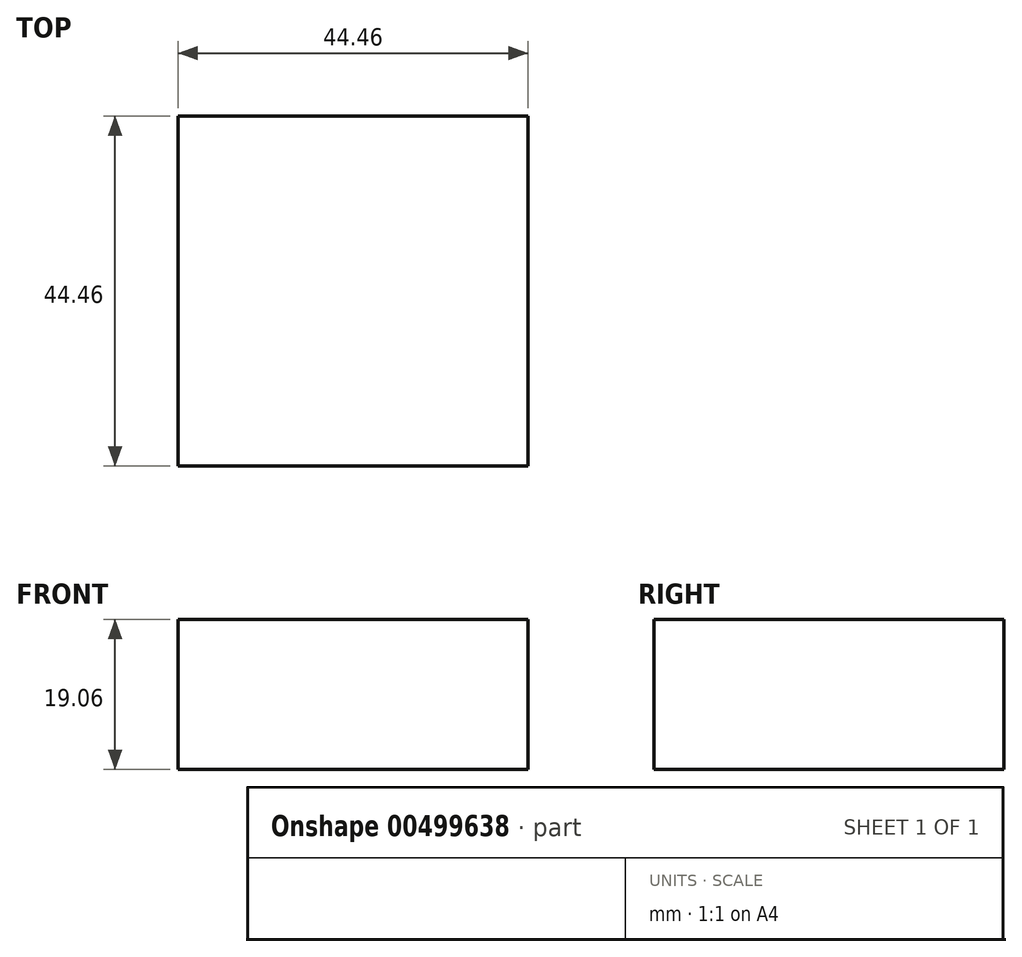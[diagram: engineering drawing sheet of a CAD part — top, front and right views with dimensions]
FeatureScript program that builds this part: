
annotation { "Feature Type Name" : "Feature", "Feature Type Description" : "" }
export const myFeature = defineFeature(function(context is Context, id is Id, definition is map)
    precondition{}
    {
        {
            var Q0;
            Q0=qCreatedBy(makeId("Front.planeOp"),FACE);
            var sketch = newSketch(context, id + "F0", { "sketchPlane" : qUnion([Q0])});
            skLineSegment(sketch, "E0.bottom", {"start": v(22.23, -9.52) * mm, "end": v(-22.23, -9.53) * mm});
            skLineSegment(sketch, "E0.top", {"start": v(22.23, 9.53) * mm, "end": v(-22.23, 9.52) * mm});
            skLineSegment(sketch, "E0.left", {"start": v(22.23, -9.52) * mm, "end": v(22.23, 9.53) * mm});
            skLineSegment(sketch, "E0.right", {"start": v(-22.23, -9.53) * mm, "end": v(-22.23, 9.52) * mm});
            skPoint(sketch, "E0.middle", {"position": v(0, 0) * mm});
            skSolve(sketch);
        }
        {
            var Q0;
            Q0 = qSketchRegion(id + "F0", true);
            extrude(context, id + "F1", {"entities" : qUnion([Q0]), "depth" : 22.22 * mm, "hasSecondDirection" : true, "secondDirectionOppositeDirection" : true, "secondDirectionDepth" : 22.22 * mm});
        }
    });
